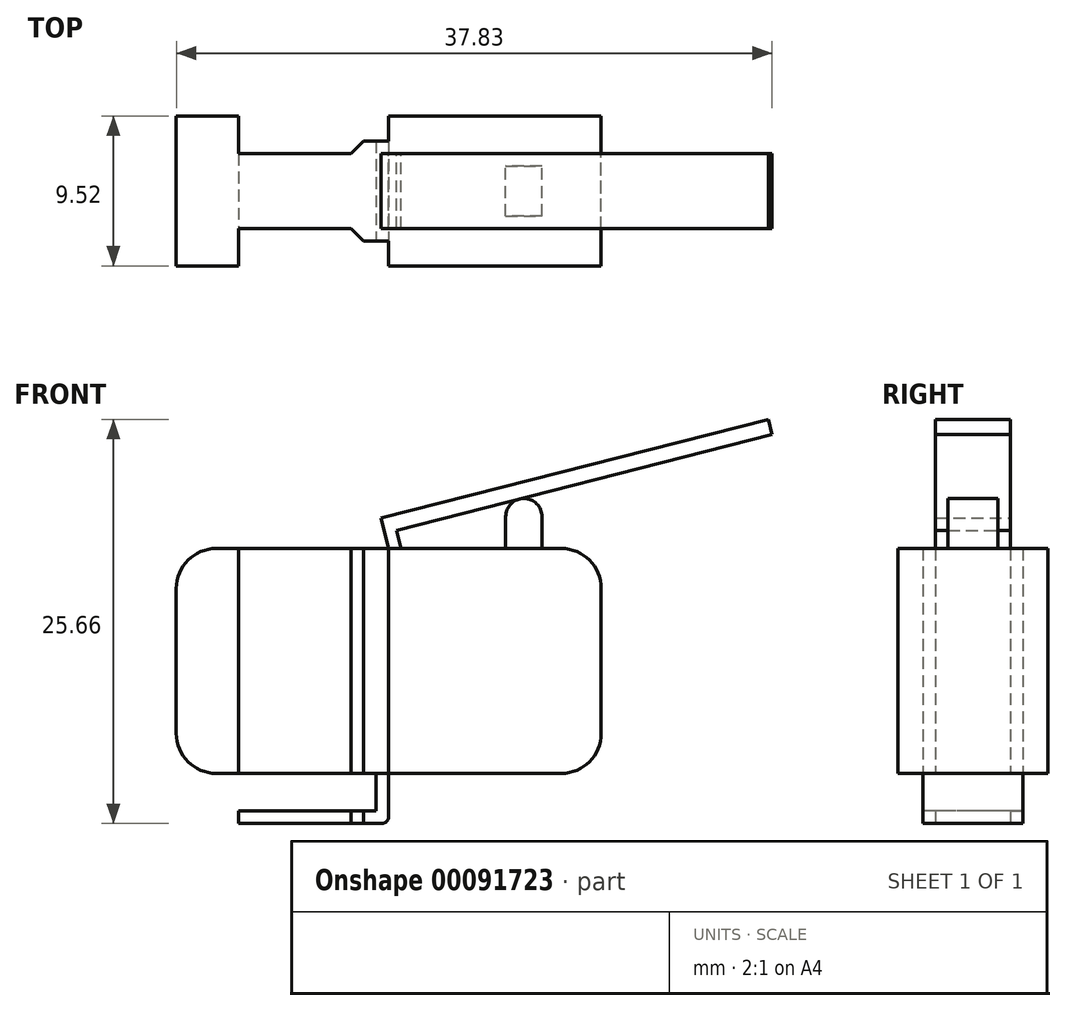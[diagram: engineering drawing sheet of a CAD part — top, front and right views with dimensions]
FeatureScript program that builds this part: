
annotation { "Feature Type Name" : "Feature", "Feature Type Description" : "" }
export const myFeature = defineFeature(function(context is Context, id is Id, definition is map)
    precondition{}
    {
        {
            var Q0;
            Q0=qCreatedBy(makeId("Front.planeOp"),FACE);
            var sketch = newSketch(context, id + "F0", { "sketchPlane" : qUnion([Q0])});
            skLineSegment(sketch, "E0.bottom", {"start": v(13.5, 7.14) * mm, "end": v(-13.5, 7.14) * mm});
            skLineSegment(sketch, "E0.top", {"start": v(13.5, -7.14) * mm, "end": v(-13.5, -7.14) * mm});
            skLineSegment(sketch, "E0.left", {"start": v(13.5, 7.14) * mm, "end": v(13.5, -7.14) * mm});
            skLineSegment(sketch, "E0.right", {"start": v(-13.5, 7.14) * mm, "end": v(-13.5, -7.14) * mm});
            skPoint(sketch, "E0.middle", {"position": v(0, 0) * mm});
            skLineSegment(sketch, "E1", {"start": v(-25.16, 7.14) * mm, "end": v(37.96, 7.14) * mm, "construction": true});
            skLineSegment(sketch, "E2", {"start": v(-26.92, -7.14) * mm, "end": v(39.63, -7.14) * mm, "construction": true});
            skSolve(sketch);
        }
        {
            var Q0;
            Q0 = qSketchRegion(id + "F0", true);
            extrude(context, id + "F1", {"entities" : qUnion([Q0]), "endBound" : BoundingType.SYMMETRIC, "depth" : 9.52 * mm});
        }
        {
            var Q0;
            Q0=qCreatedBy(makeId("Front.planeOp"),FACE);
            var sketch = newSketch(context, id + "F2", { "sketchPlane" : qUnion([Q0])});
            skLineSegment(sketch, "E3.bottom", {"start": v(7.43, 7.14) * mm, "end": v(9.73, 7.14) * mm});
            skLineSegment(sketch, "E3.top", {"start": v(7.43, 9.16) * mm, "end": v(9.73, 9.16) * mm});
            skLineSegment(sketch, "E3.left", {"start": v(7.43, 7.14) * mm, "end": v(7.43, 9.16) * mm});
            skLineSegment(sketch, "E3.right", {"start": v(9.73, 7.14) * mm, "end": v(9.73, 9.16) * mm});
            skArc(sketch, "E4", {"start": v(9.73, 9.16) * mm, "mid": v(8.58, 10.32) * mm, "end": v(7.43, 9.16) * mm});
            skSolve(sketch);
        }
        {
            var Q0;
            Q0 = qSketchRegion(id + "F2", true);
            extrude(context, id + "F3", {"entities" : qUnion([Q0]), "operationType" : NewBodyOperationType.ADD, "endBound" : BoundingType.SYMMETRIC, "depth" : 3.17 * mm});
        }
        {
            var Q0;
            Q0=makeQuery(id+"F1.opExtrude","SWEPT_EDGE",EDGE,{"disambiguationData":[OSD([sQuery(id+"F0.wireOp",EDGE,"E0.bottom"),sQuery(id+"F0.wireOp",EDGE,"E0.left")])]});
            var Q1;
            Q1=makeQuery(id+"F1.opExtrude","SWEPT_EDGE",EDGE,{"disambiguationData":[OSD([sQuery(id+"F0.wireOp",EDGE,"E0.bottom"),sQuery(id+"F0.wireOp",EDGE,"E0.right")])]});
            var Q2;
            Q2=makeQuery(id+"F1.opExtrude","SWEPT_EDGE",EDGE,{"disambiguationData":[OSD([sQuery(id+"F0.wireOp",EDGE,"E0.top"),sQuery(id+"F0.wireOp",EDGE,"E0.left")])]});
            var Q3;
            Q3=makeQuery(id+"F1.opExtrude","SWEPT_EDGE",EDGE,{"disambiguationData":[OSD([sQuery(id+"F0.wireOp",EDGE,"E0.top"),sQuery(id+"F0.wireOp",EDGE,"E0.right")])]});
            fillet(context, id + "F4", {"entities" : qUnion([Q0, Q1, Q2, Q3]), "radius" : 2.54 * mm, "tangentPropagation" : true, "allowEdgeOverflow" : false});
        }
        {
            var Q0;
            Q0=qCreatedBy(makeId("Front.planeOp"),FACE);
            var sketch = newSketch(context, id + "F5", { "sketchPlane" : qUnion([Q0])});
            skLineSegment(sketch, "E5", {"start": v(0.8, 7.14) * mm, "end": v(0.5, 8.3) * mm});
            skLineSegment(sketch, "E6", {"start": v(-0.49, 9.07) * mm, "end": v(24.12, 15.34) * mm});
            skLineSegment(sketch, "E7", {"start": v(0.5, 8.3) * mm, "end": v(24.34, 14.37) * mm});
            skLineSegment(sketch, "E8", {"start": v(24.12, 15.34) * mm, "end": v(24.34, 14.37) * mm});
            skLineSegment(sketch, "E9", {"start": v(0, 7.14) * mm, "end": v(0.8, 7.14) * mm});
            skLineSegment(sketch, "E10", {"start": v(-0.49, 9.07) * mm, "end": v(0, 7.14) * mm});
            skSolve(sketch);
        }
        {
            var Q0;
            Q0=makeQuery(id+"F1.opExtrude","CAP_FACE",FACE,{"disambiguationData":[OSD([sQuery(id+"F0.wireOp",EDGE,"E0.bottom"),sQuery(id+"F0.wireOp",EDGE,"E0.top"),sQuery(id+"F0.wireOp",EDGE,"E0.left"),sQuery(id+"F0.wireOp",EDGE,"E0.right")])],"isStart":false});
            var sketch = newSketch(context, id + "F6", { "sketchPlane" : qUnion([Q0])});
            skLineSegment(sketch, "E11", {"start": v(-0.8, -7.14) * mm, "end": v(-0.8, -9.53) * mm});
            skLineSegment(sketch, "E12", {"start": v(0, -7.14) * mm, "end": v(0, -10.32) * mm});
            skLineSegment(sketch, "E13", {"start": v(-0.8, -9.53) * mm, "end": v(-9.52, -9.53) * mm});
            skLineSegment(sketch, "E14", {"start": v(0, -10.32) * mm, "end": v(-9.52, -10.32) * mm});
            skLineSegment(sketch, "E15", {"start": v(-9.52, -9.53) * mm, "end": v(-9.52, -10.32) * mm});
            skSolve(sketch);
        }
        {
            var Q0;
            {var subQ1=sQuery(id+"F6.wireOp",EDGE,"E11");Q0=makeQuery(id+"F6.imprint","IMPRINT",FACE,{"disambiguationData":[TD([[makeQuery(id+"F6.imprint","IMPRINT",EDGE,{"derivedFrom":subQ1}),1.0]])]});}
            extrude(context, id + "F7", {"entities" : qUnion([Q0]), "oppositeDirection" : true, "depth" : 9.52 * mm});
        }
        {
            var Q0;
            Q0 = qSketchRegion(id + "F5", true);
            extrude(context, id + "F8", {"entities" : qUnion([Q0]), "endBound" : BoundingType.SYMMETRIC, "depth" : 4.76 * mm});
        }
        {
            var Q0;
            Q0=makeQuery(id+"F7.opExtrude","SWEPT_FACE",FACE,{"disambiguationData":[OSD([sQuery(id+"F6.wireOp",EDGE,"E14")])]});
            var sketch = newSketch(context, id + "F9", { "sketchPlane" : qUnion([Q0])});
            skLineSegment(sketch, "E16", {"start": v(-1.59, 4.76) * mm, "end": v(-1.59, -4.76) * mm});
            skLineSegment(sketch, "E17", {"start": v(-9.52, 2.38) * mm, "end": v(0, 2.38) * mm});
            skLineSegment(sketch, "E18", {"start": v(-9.52, -2.38) * mm, "end": v(0, -2.38) * mm});
            skLineSegment(sketch, "E19", {"start": v(0, -3.17) * mm, "end": v(-1.59, -3.17) * mm});
            skLineSegment(sketch, "E20", {"start": v(0, 3.17) * mm, "end": v(-1.59, 3.17) * mm});
            skLineSegment(sketch, "E21", {"start": v(-1.59, -3.17) * mm, "end": v(-2.38, -2.38) * mm});
            skLineSegment(sketch, "E22", {"start": v(-1.59, 3.17) * mm, "end": v(-2.38, 2.38) * mm});
            skSolve(sketch);
        }
        {
            var Q0;
            {var subQ0=sQuery(id+"F9.wireOp",EDGE,"E16");var subQ1=sQuery(id+"F6.wireOp",EDGE,"E14");var subQ2=makeQuery(id+"F7.opExtrude","CAP_EDGE",EDGE,{"disambiguationData":[OSD([subQ1])],"isStart":true});var subQ3=makeQuery(id+"F9.imprint","INTERSECT",VERTEX,{"derivedFrom":[subQ2,subQ0]});Q0=makeQuery(id+"F9.imprint","IMPRINT",FACE,{"disambiguationData":[TD([[makeQuery(id+"F9.imprint","IMPRINT",EDGE,{"disambiguationData":[TD([[subQ3,-1.0]])],"derivedFrom":subQ0}),1.0]])]});}
            var Q1;
            {var subQ8=sQuery(id+"F9.wireOp",EDGE,"E22");Q1=makeQuery(id+"F9.imprint","IMPRINT",FACE,{"disambiguationData":[TD([[makeQuery(id+"F9.imprint","IMPRINT",EDGE,{"derivedFrom":subQ8}),-1.0]])]});}
            var Q2;
            {var subQ4=sQuery(id+"F9.wireOp",EDGE,"E21");Q2=makeQuery(id+"F9.imprint","IMPRINT",FACE,{"disambiguationData":[TD([[makeQuery(id+"F9.imprint","IMPRINT",EDGE,{"derivedFrom":subQ4}),1.0]])]});}
            var Q3;
            {var subQ0=sQuery(id+"F9.wireOp",EDGE,"E16");var subQ1=sQuery(id+"F6.wireOp",EDGE,"E14");var subQ2=makeQuery(id+"F7.opExtrude","CAP_EDGE",EDGE,{"disambiguationData":[OSD([subQ1])],"isStart":false});var subQ3=makeQuery(id+"F9.imprint","INTERSECT",VERTEX,{"derivedFrom":[subQ2,subQ0]});Q3=makeQuery(id+"F9.imprint","IMPRINT",FACE,{"disambiguationData":[TD([[makeQuery(id+"F9.imprint","IMPRINT",EDGE,{"disambiguationData":[TD([[subQ3,1.0]])],"derivedFrom":subQ0}),1.0]])]});}
            extrude(context, id + "F10", {"entities" : qUnion([Q0, Q1, Q2, Q3]), "operationType" : NewBodyOperationType.REMOVE, "endBound" : BoundingType.THROUGH_ALL, "oppositeDirection" : true, "depth" : 25.4 * mm});
        }
        {
            var Q0;
            Q0=makeQuery(id+"F7.opExtrude","SWEPT_EDGE",EDGE,{"disambiguationData":[OSD([sQuery(id+"F6.wireOp",EDGE,"E12"),sQuery(id+"F6.wireOp",EDGE,"E14")])]});
            fillet(context, id + "F11", {"entities" : qUnion([Q0]), "radius" : 0.43 * mm, "tangentPropagation" : true, "allowEdgeOverflow" : false});
        }
    });
